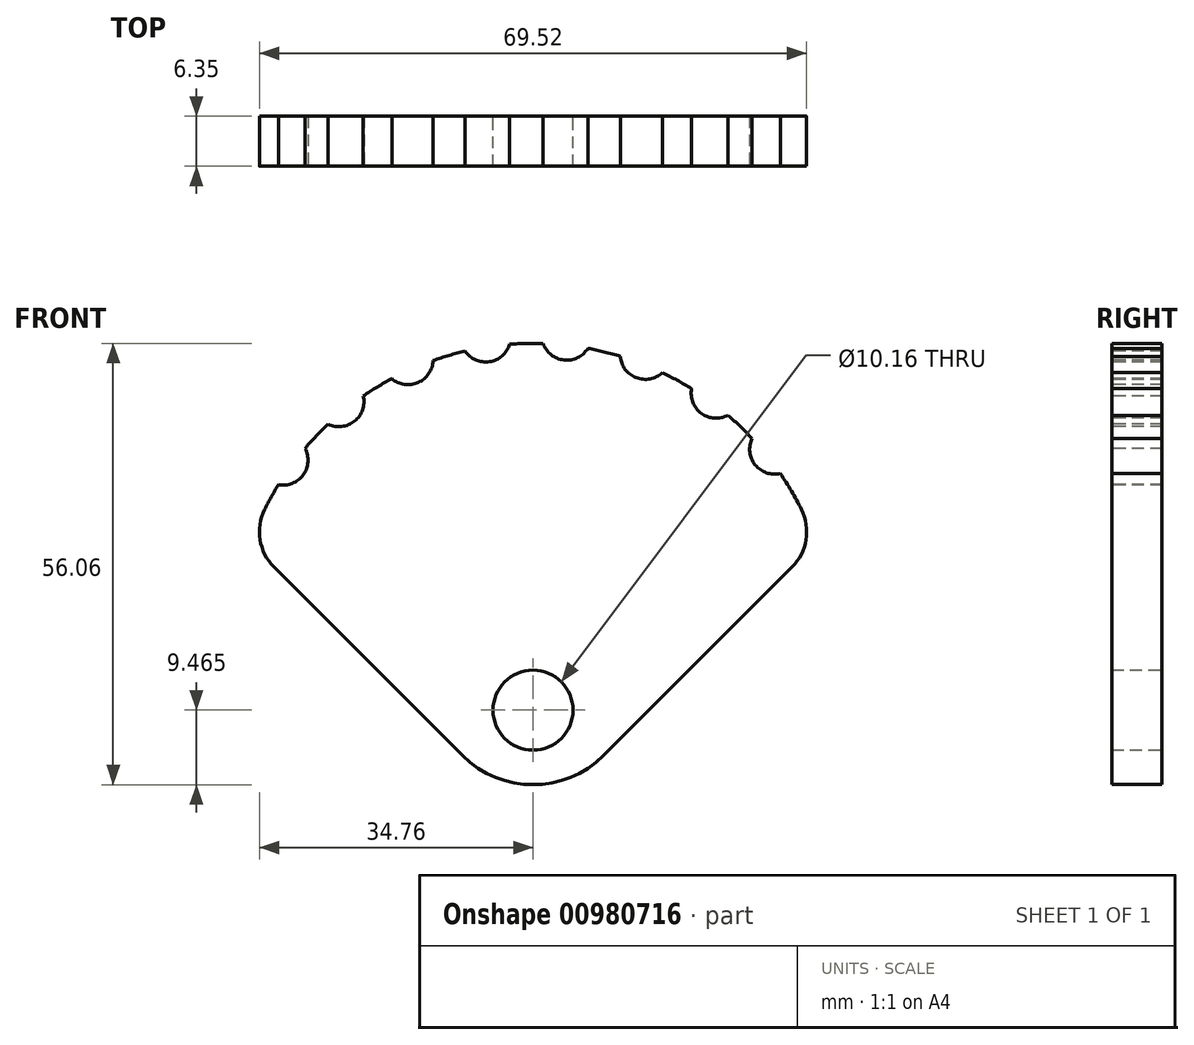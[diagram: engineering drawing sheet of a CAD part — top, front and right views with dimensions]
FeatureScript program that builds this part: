
annotation { "Feature Type Name" : "Feature", "Feature Type Description" : "" }
export const myFeature = defineFeature(function(context is Context, id is Id, definition is map)
    precondition{}
    {
        {
            var Q0;
            Q0=qCreatedBy(makeId("Front.planeOp"),FACE);
            var sketch = newSketch(context, id + "F0", { "sketchPlane" : qUnion([Q0])});
            skLineSegment(sketch, "E0", {"start": v(-8.98, -29.12) * mm, "end": v(-32.9, -5.2) * mm});
            skLineSegment(sketch, "E1", {"start": v(8.98, -29.12) * mm, "end": v(32.9, -5.2) * mm});
            skArc(sketch, "E2", {"start": v(34.1, 2.13) * mm, "mid": v(0, 23.22) * mm, "end": v(-34.1, 2.13) * mm});
            skPoint(sketch, "E3.visualSharp", {"position": v(-35.92, -2.18) * mm});
            skArc(sketch, "E3.filletArc", {"start": v(-34.1, 2.13) * mm, "mid": v(-34.68, -1.73) * mm, "end": v(-32.9, -5.2) * mm});
            skPoint(sketch, "E4.visualSharp", {"position": v(35.92, -2.18) * mm});
            skArc(sketch, "E4.filletArc", {"start": v(32.9, -5.2) * mm, "mid": v(34.68, -1.73) * mm, "end": v(34.1, 2.13) * mm});
            skPoint(sketch, "E5.visualSharp", {"position": v(0, -38.1) * mm});
            skArc(sketch, "E5.filletArc", {"start": v(-8.98, -29.12) * mm, "mid": v(0, -32.84) * mm, "end": v(8.98, -29.12) * mm});
            skCircle(sketch, "E6", {"center": v(0, -23.37) * mm, "radius": 5.08 * mm});
            skSolve(sketch);
        }
        {
            var Q0;
            Q0=makeQuery(id+"F0.imprint","IMPRINT",FACE,{"disambiguationData":[TD([[makeQuery(id+"F0.imprint","IMPRINT",EDGE,{"derivedFrom":sQuery(id+"F0.wireOp",EDGE,"E0")}),-1.0]])]});
            extrude(context, id + "F1", {"entities" : qUnion([Q0]), "depth" : 6.35 * mm, "offsetDistance" : 25.4 * mm});
        }
        {
            var Q0;
            Q0=makeQuery(id+"F1.opExtrude","CAP_FACE",FACE,{"disambiguationData":[OSD([sQuery(id+"F0.wireOp",EDGE,"E0"),sQuery(id+"F0.wireOp",EDGE,"E1"),sQuery(id+"F0.wireOp",EDGE,"E2"),sQuery(id+"F0.wireOp",EDGE,"E3.filletArc"),sQuery(id+"F0.wireOp",EDGE,"E4.filletArc"),sQuery(id+"F0.wireOp",EDGE,"E5.filletArc"),sQuery(id+"F0.wireOp",EDGE,"E6")])],"isStart":false});
            var sketch = newSketch(context, id + "F2", { "sketchPlane" : qUnion([Q0])});
            skLineSegment(sketch, "E7", {"start": v(0, -23.37) * mm, "end": v(-63.52, 40.15) * mm, "construction": true});
            skCircle(sketch, "E8", {"center": v(-31.76, 8.39) * mm, "radius": 3.18 * mm});
            skLineSegment(sketch, "E9", {"start": v(0, -23.37) * mm, "end": v(42.26, 22.65) * mm, "construction": true});
            skCircle(sketch, "E10.1.0", {"center": v(-24.66, 15.81) * mm, "radius": 3.18 * mm});
            skCircle(sketch, "E10.2.0", {"center": v(-15.87, 21.15) * mm, "radius": 3.18 * mm});
            skCircle(sketch, "E10.3.0", {"center": v(-6, 24.03) * mm, "radius": 3.18 * mm});
            skCircle(sketch, "E10.4.0", {"center": v(4.27, 24.26) * mm, "radius": 3.18 * mm});
            skCircle(sketch, "E10.5.0", {"center": v(14.25, 21.82) * mm, "radius": 3.18 * mm});
            skCircle(sketch, "E10.6.0", {"center": v(23.26, 16.88) * mm, "radius": 3.18 * mm});
            skCircle(sketch, "E10.7.0", {"center": v(30.7, 9.78) * mm, "radius": 3.18 * mm});
            skPoint(sketch, "E10.center", {"position": v(0, -14.88) * mm});
            skLineSegment(sketch, "E10.anchor1", {"start": v(0, -14.88) * mm, "end": v(-31.76, 8.39) * mm, "construction": true});
            skLineSegment(sketch, "E10.anchor2", {"start": v(0, -14.88) * mm, "end": v(30.7, 9.78) * mm, "construction": true});
            skSolve(sketch);
        }
        {
            var Q0;
            Q0 = qSketchRegion(id + "F2", true);
            extrude(context, id + "F3", {"entities" : qUnion([Q0]), "operationType" : NewBodyOperationType.REMOVE, "oppositeDirection" : true, "depth" : 25.4 * mm, "offsetDistance" : 25.4 * mm});
        }
    });
